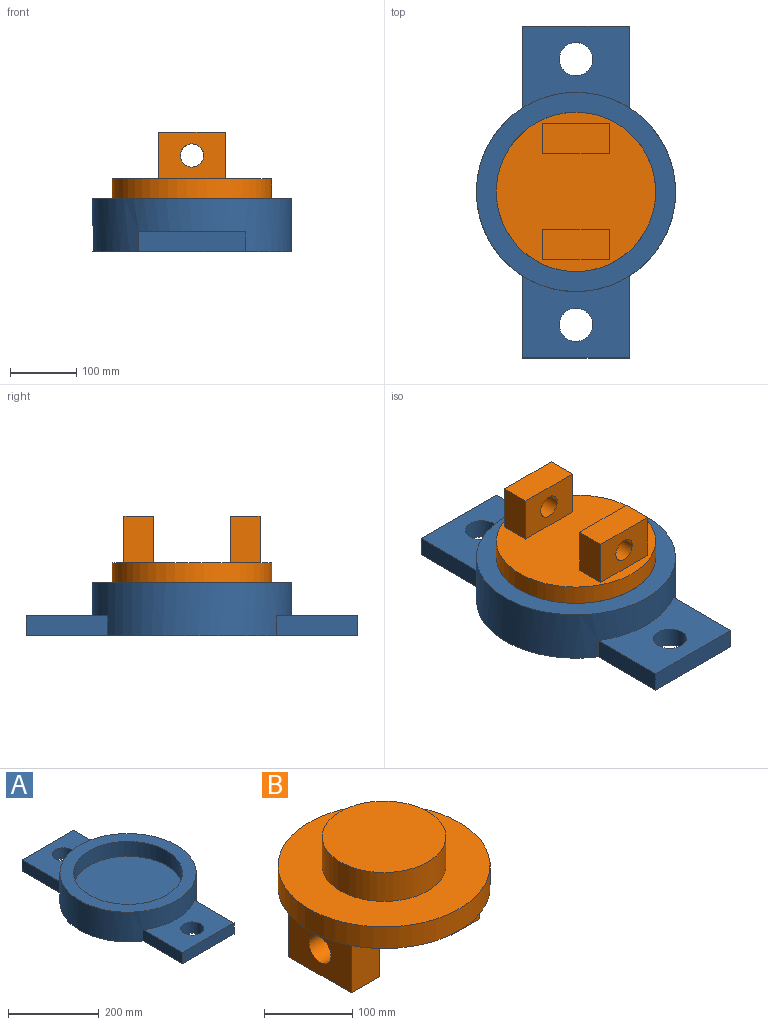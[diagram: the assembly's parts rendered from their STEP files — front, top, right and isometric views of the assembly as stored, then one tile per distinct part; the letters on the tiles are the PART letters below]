
ASSEMBLY  parts=2 mates=1
PART A: 15 faces, bbox 300x500x80 mm
  f0: cylinder r=150mm len=300mm, axis (0,0,-1), area 65272.6mm2, adj f1,f3,f7,f8,f9,f10,f11,f13
  f1: plane 500x300mm, normal (0,0,-1), area 101143mm2, adj f0,f5,f6,f8,f9,f11,f12,f13
  f2: cylinder r=120mm len=240mm, axis (0,0,-1), area 30159.3mm2, adj f3,f4
  f3: plane 300x300mm, normal (0,0,1), area 25446.9mm2, adj f0,f2
  f4: plane 240x240mm, normal (0,0,1), area 45238.9mm2, adj f2
  f5: cylinder r=25mm len=50mm, axis (0,0,-1), area 4712.4mm2, adj f1,f7
  f6: plane 160x30mm, normal (0,-1,0), area 4800mm2, adj f1,f7,f8,f9
  f7: plane 160x123.11mm, normal (0,0,1), area 15228.6mm2, adj f0,f5,f6,f8,f9
  f8: plane 123.11x30mm, normal (-1,0,0), area 3693.4mm2, adj f0,f1,f6,f7
  f9: plane 123.11x30mm, normal (1,0,0), area 3693.4mm2, adj f0,f1,f6,f7
  f10: plane 160x123.11mm, normal (0,0,1), area 15228.6mm2, adj f0,f11,f12,f13,f14
  f11: plane 123.11x30mm, normal (1,0,0), area 3693.4mm2, adj f0,f1,f10,f12
  f12: plane 160x30mm, normal (0,1,0), area 4800mm2, adj f1,f10,f11,f13
  f13: plane 123.11x30mm, normal (-1,0,0), area 3693.4mm2, adj f0,f1,f10,f12
  f14: cylinder r=25mm len=50mm, axis (0,0,-1), area 4712.4mm2, adj f1,f10
PART B: 17 faces, bbox 240x240x140 mm
  f0: cylinder r=70mm len=140mm, axis (0,0,-1), area 17592.9mm2, adj f1,f3
  f1: plane 140x140mm, normal (0,0,1), area 15393.8mm2, adj f0
  f2: cylinder r=120mm len=240mm, axis (0,0,-1), area 22619.5mm2, adj f3,f4
  f3: plane 240x240mm, normal (0,0,1), area 29845.1mm2, adj f0,f2
  f4: plane 240x240mm, normal (0,0,-1), area 36238.9mm2, adj f2,f5,f6,f7,f8,f10,f11,f12
  f5: plane 100x70mm, normal (-1,0,0), area 6037.9mm2, adj f4,f6,f8,f9,f16
  f6: plane 70x45mm, normal (0,-1,0), area 3150mm2, adj f4,f5,f7,f9
  f7: plane 100x70mm, normal (1,0,0), area 6037.9mm2, adj f4,f6,f8,f9,f16
  f8: plane 70x45mm, normal (0,1,0), area 3150mm2, adj f4,f5,f7,f9
  f9: plane 100x45mm, normal (0,0,-1), area 4500mm2, adj f5,f6,f7,f8
  f10: plane 100x70mm, normal (1,0,0), area 6037.9mm2, adj f4,f11,f13,f14,f15
  f11: plane 70x45mm, normal (0,1,0), area 3150mm2, adj f4,f10,f12,f14
  f12: plane 100x70mm, normal (-1,0,0), area 6037.9mm2, adj f4,f11,f13,f14,f15
  f13: plane 70x45mm, normal (0,-1,0), area 3150mm2, adj f4,f10,f12,f14
  f14: plane 100x45mm, normal (0,0,-1), area 4500mm2, adj f10,f11,f12,f13
  f15: cylinder r=17.5mm len=45mm, axis (1,0,0), area 4948mm2, adj f10,f12
  f16: cylinder r=17.5mm len=45mm, axis (1,0,0), area 4948mm2, adj f5,f7
PLACE A at identity fixed
PLACE B rot(axis=(0.71,0.71,0),180deg) t=(0,0,110)mm
MATE revolute B.f0 <-> A.f2  axis (0,0,-1) through (0,0,40)mm
